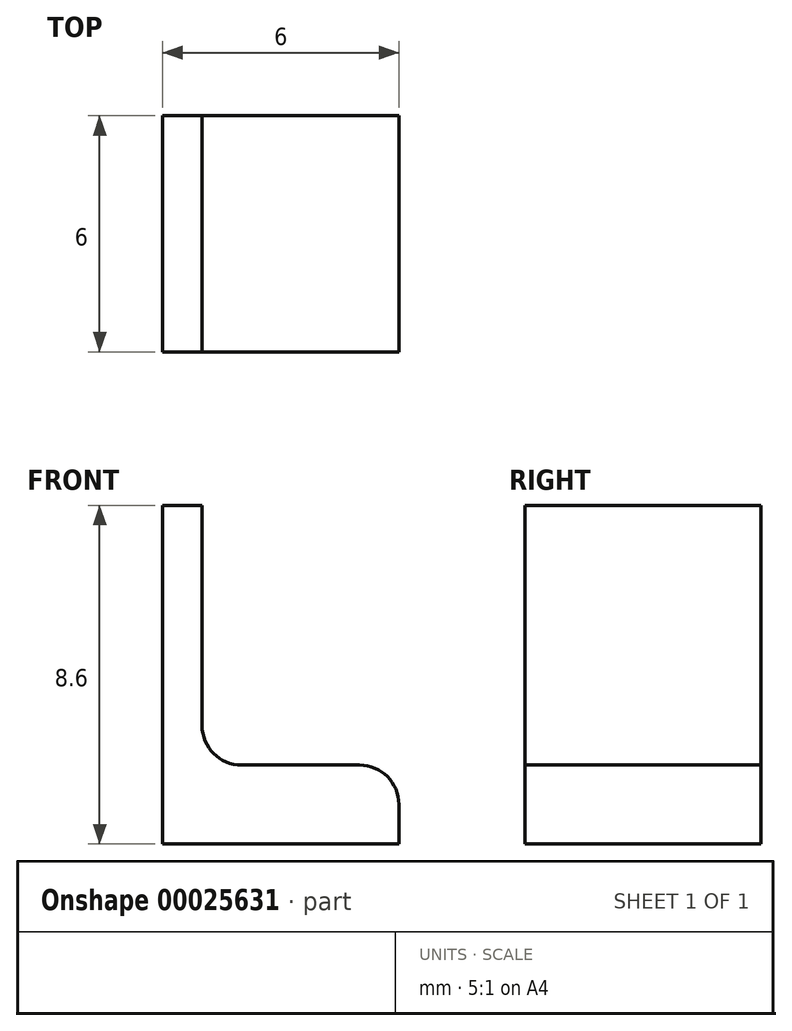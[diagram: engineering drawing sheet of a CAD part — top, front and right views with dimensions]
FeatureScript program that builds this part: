
annotation { "Feature Type Name" : "Feature", "Feature Type Description" : "" }
export const myFeature = defineFeature(function(context is Context, id is Id, definition is map)
    precondition{}
    {
        {
            var Q0;
            Q0=qCreatedBy(makeId("Front.planeOp"),FACE);
            var sketch = newSketch(context, id + "F0", { "sketchPlane" : qUnion([Q0])});
            skLineSegment(sketch, "E0.bottom", {"start": v(0, 8.6) * mm, "end": v(1, 8.6) * mm});
            skLineSegment(sketch, "E0.top", {"start": v(0, 0) * mm, "end": v(1, 0) * mm});
            skLineSegment(sketch, "E0.left", {"start": v(0, 8.6) * mm, "end": v(0, 0) * mm});
            skLineSegment(sketch, "E0.right", {"start": v(1, 8.6) * mm, "end": v(1, 2) * mm});
            skLineSegment(sketch, "E1.bottom", {"start": v(1, 0) * mm, "end": v(6, 0) * mm});
            skLineSegment(sketch, "E1.top", {"start": v(1, 2) * mm, "end": v(6, 2) * mm});
            skLineSegment(sketch, "E1.right", {"start": v(6, 0) * mm, "end": v(6, 2) * mm});
            skSolve(sketch);
        }
        {
            var Q0;
            Q0 = qSketchRegion(id + "F0", true);
            extrude(context, id + "F1", {"entities" : qUnion([Q0]), "depth" : 6 * mm});
        }
        {
            var Q0;
            Q0=makeQuery(id+"F1.opExtrude","SWEPT_EDGE",EDGE,{"disambiguationData":[OSD([sQuery(id+"F0.wireOp",EDGE,"E0.right"),sQuery(id+"F0.wireOp",EDGE,"E1.top")])]});
            var Q1;
            Q1=makeQuery(id+"F1.opExtrude","SWEPT_EDGE",EDGE,{"disambiguationData":[OSD([sQuery(id+"F0.wireOp",EDGE,"E1.top"),sQuery(id+"F0.wireOp",EDGE,"E1.right")])]});
            fillet(context, id + "F2", {"entities" : qUnion([Q0, Q1]), "radius" : 1 * mm, "tangentPropagation" : true, "allowEdgeOverflow" : false});
        }
    });
